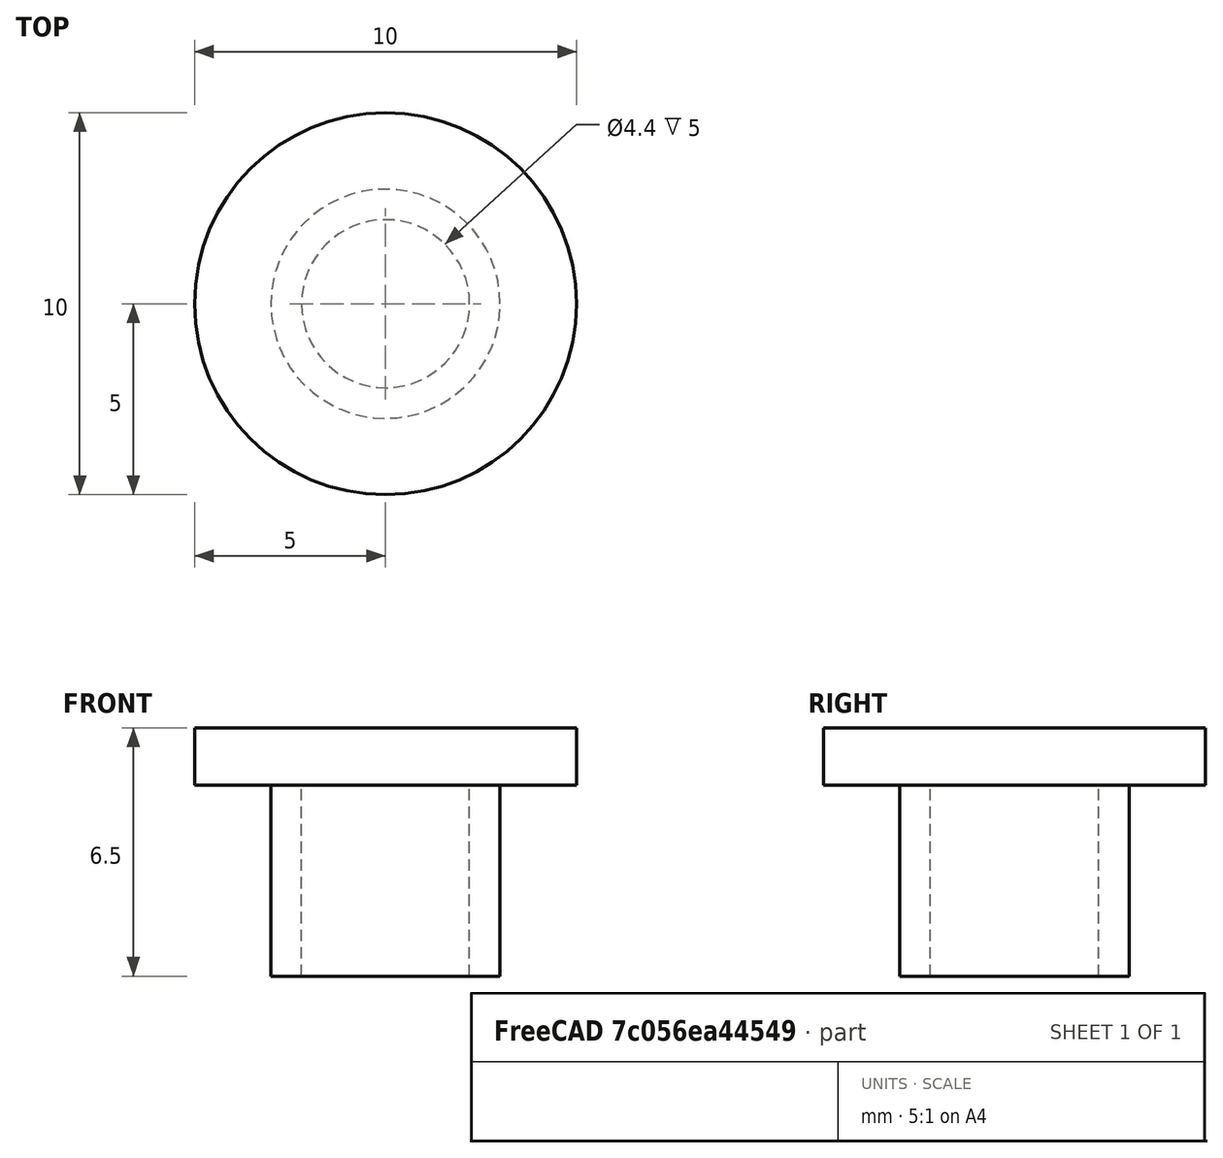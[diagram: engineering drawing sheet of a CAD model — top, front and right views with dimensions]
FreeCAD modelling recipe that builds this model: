
FCSTD DOCUMENT  (FreeCAD 0.19R24291 (Git))
Label: eth_conn_top_plug_1
License: All rights reserved
LicenseURL: http://en.wikipedia.org/wiki/All_rights_reserved
objects: Part::Cylinder×3, Part::Cut×1, Part::MultiFuse×1, Part::Refine×1
note: 6 computed .brp shape members not serialized (recipe doc carries the construction recipe); baked Part::Feature solids carry a one-line shape summary decoded from their .brp

FEATURE [Part::Cylinder] Cylinder
  Angle = 360
  AttacherType = Attacher::AttachEngine3D
  Height = 5
  Radius = 3
FEATURE [Part::Cylinder] Cylinder001
  Angle = 360
  AttacherType = Attacher::AttachEngine3D
  Height = 1.5
  Placement = pos=(0,0,5) rot=(0,0,1;0rad)
  Radius = 5
FEATURE [Part::Cylinder] Cylinder002
  Angle = 360
  AttacherType = Attacher::AttachEngine3D
  Height = 5
  Radius = 2.2
FEATURE [Part::Cut] Cut
  Base = -> Cylinder
  Tool = -> Cylinder002
FEATURE [Part::MultiFuse] Fusion
  Shapes = -> [Cut,Cylinder001]
FEATURE [Part::Refine] Fusion001
  Source = -> Fusion
